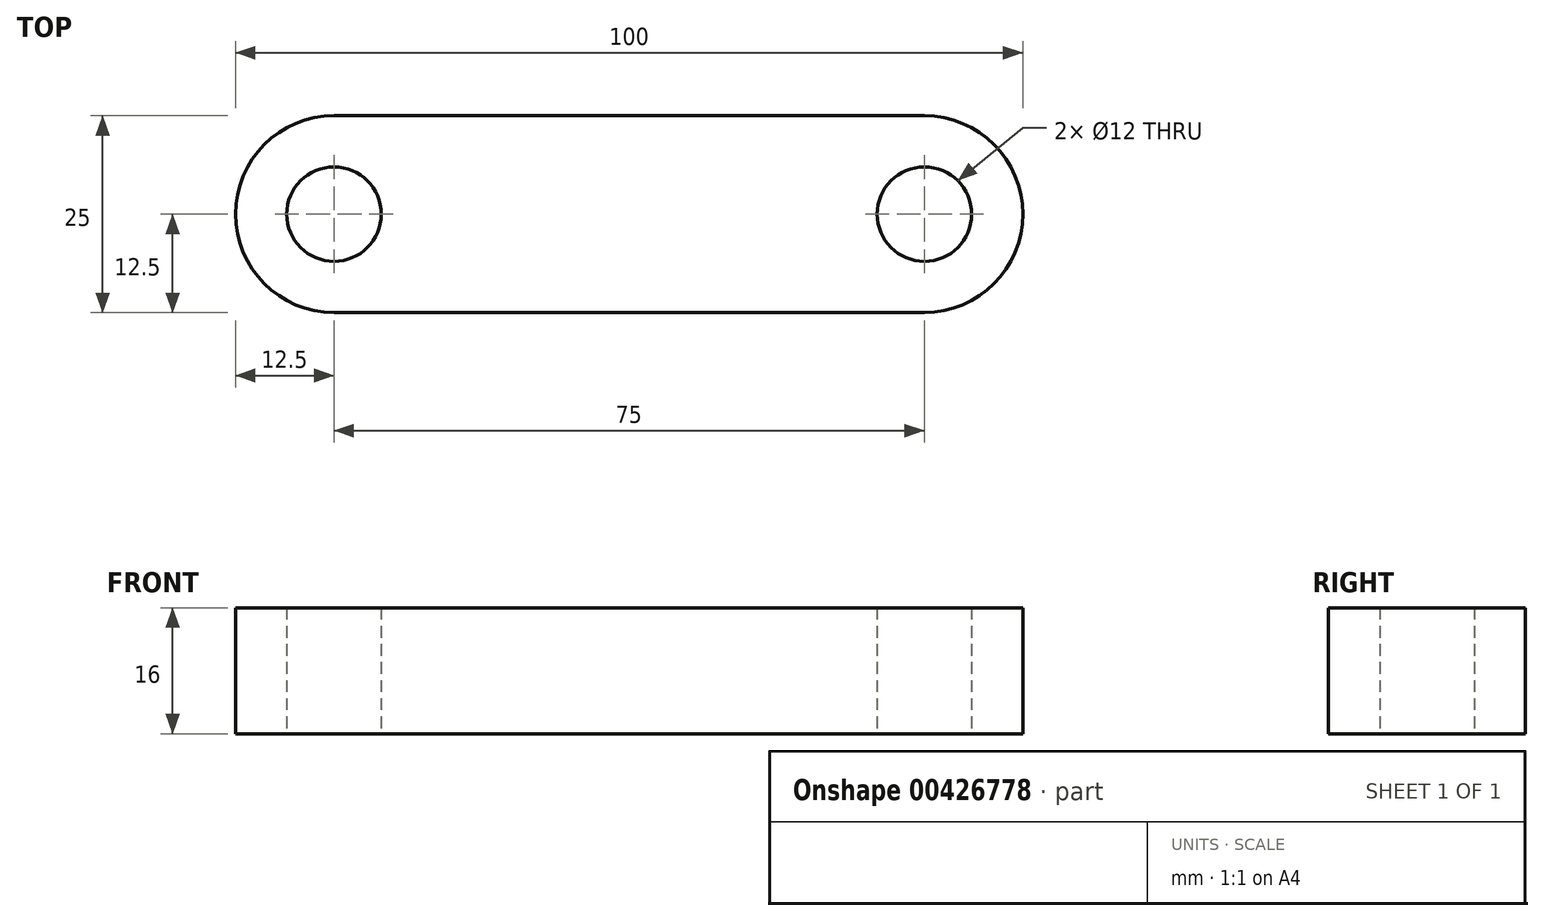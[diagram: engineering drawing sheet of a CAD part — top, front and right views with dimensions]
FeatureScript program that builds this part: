
annotation { "Feature Type Name" : "Feature", "Feature Type Description" : "" }
export const myFeature = defineFeature(function(context is Context, id is Id, definition is map)
    precondition{}
    {
        {
            var Q0;
            Q0=qCreatedBy(makeId("Top.planeOp"),FACE);
            var sketch = newSketch(context, id + "F0", { "sketchPlane" : qUnion([Q0])});
            skLineSegment(sketch, "E0.bottom", {"start": v(-12.5, 12.5) * mm, "end": v(87.5, 12.5) * mm});
            skLineSegment(sketch, "E0.top", {"start": v(-12.5, -12.5) * mm, "end": v(87.5, -12.5) * mm});
            skLineSegment(sketch, "E0.left", {"start": v(-12.5, 12.5) * mm, "end": v(-12.5, -12.5) * mm});
            skCircle(sketch, "E1", {"center": v(0, 0) * mm, "radius": 12.5 * mm});
            skPoint(sketch, "E1.centerSnap0", {"position": v(-12.5, 0) * mm});
            skCircle(sketch, "E2", {"center": v(0, 0) * mm, "radius": 6 * mm});
            skPoint(sketch, "E3.visualSharp", {"position": v(87.5, -12.5) * mm});
            skCircle(sketch, "E4", {"center": v(75, 0) * mm, "radius": 6 * mm});
            skLineSegment(sketch, "E5", {"start": v(87.5, -12.5) * mm, "end": v(87.5, 12.5) * mm});
            skCircle(sketch, "E6", {"center": v(75, 0) * mm, "radius": 12.5 * mm});
            skPoint(sketch, "E6.centerSnap0", {"position": v(87.5, 0) * mm});
            skSolve(sketch);
        }
        {
            var Q0;
            {var subQ0=sQuery(id+"F0.wireOp",EDGE,"E1");var subQ1=sQuery(id+"F0.wireOp",EDGE,"E0.bottom");var subQ2=makeQuery(id+"F0.imprint","INTERSECT",VERTEX,{"derivedFrom":[subQ1,subQ0]});Q0=makeQuery(id+"F0.imprint","IMPRINT",FACE,{"disambiguationData":[TD([[makeQuery(id+"F0.imprint","IMPRINT",EDGE,{"disambiguationData":[TD([[subQ2,-1.0]])],"derivedFrom":subQ1}),-1.0]])]});}
            var Q1;
            {var subQ5=sQuery(id+"F0.wireOp",EDGE,"XRnApHOD-x3u0-sg9e-AL6Z-4tSMUb5GBw0s.top");Q1=makeQuery(id+"F0.imprint","IMPRINT",FACE,{"disambiguationData":[TD([[makeQuery(id+"F0.imprint","IMPRINT",EDGE,{"derivedFrom":subQ5}),1.0]])]});}
            var Q2;
            {var subQ0=sQuery(id+"F0.wireOp",EDGE,"XRnApHOD-x3u0-sg9e-AL6Z-4tSMUb5GBw0s.right");var subQ1=sQuery(id+"F0.wireOp",EDGE,"E0.bottom");var subQ2=makeQuery(id+"F0.imprint","INTERSECT",VERTEX,{"derivedFrom":[subQ1,subQ0]});Q2=makeQuery(id+"F0.imprint","IMPRINT",FACE,{"disambiguationData":[TD([[makeQuery(id+"F0.imprint","IMPRINT",EDGE,{"disambiguationData":[TD([[subQ2,1.0]])],"derivedFrom":subQ1}),1.0]])]});}
            var Q3;
            Q3=makeQuery(id+"F0.imprint","IMPRINT",FACE,{"disambiguationData":[TD([[makeQuery(id+"F0.imprint","IMPRINT",EDGE,{"derivedFrom":sQuery(id+"F0.wireOp",EDGE,"E2")}),-1.0]])]});
            var Q4;
            Q4=makeQuery(id+"F0.imprint","IMPRINT",FACE,{"disambiguationData":[TD([[makeQuery(id+"F0.imprint","IMPRINT",EDGE,{"derivedFrom":sQuery(id+"F0.wireOp",EDGE,"ef2lqON3-lv6f-KqkU-rNLa-GEhmeb6gecta")}),-1.0]])]});
            var Q5;
            Q5=makeQuery(id+"F0.imprint","IMPRINT",FACE,{"disambiguationData":[TD([[makeQuery(id+"F0.imprint","IMPRINT",EDGE,{"derivedFrom":sQuery(id+"F0.wireOp",EDGE,"E4")}),-1.0]])]});
            extrude(context, id + "F1", {"entities" : qUnion([Q0, Q1, Q2, Q3, Q4, Q5]), "depth" : 16 * mm});
        }
    });
